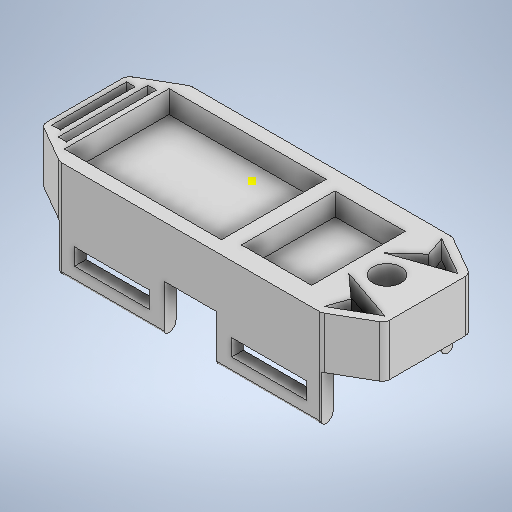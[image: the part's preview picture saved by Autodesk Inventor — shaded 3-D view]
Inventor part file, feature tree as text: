
AUTODESK INVENTOR PART (.ipt)
format: ipt  version: 2025.1 (Build 291241000, 241)  size: 457,216 bytes
history: native  units: mm
features: extrude x6, sketch x6, fillet x3
ambient origin geometry x8: Origin, YZ Plane, XZ Plane, XY Plane, X Axis, Y Axis, Z Axis, Center Point
bodies: Solid1 (feature_tree)
feature tree (15):
  extrude  "Extrusion1"  Depth=140.0mm
  sketch  "Sketch2"  dims[d9=30.0deg d10=30.0deg]
  sketch  "Sketch3"  dims[d11=25.0mm d12=25.0mm]
  extrude  "Extrusion2"  TaperAngle=30.0deg  [1 undecoded]
  extrude  "Extrusion3"  Depth=25.0mm
  extrude  "Extrusion4"  TaperAngle=150.0deg  [1 undecoded]
  extrude  "Extrusion5"  Depth=25.0mm
  extrude  "Extrusion6"  Depth=2.0mm
  fillet  "Fillet1"  Radius=84.0mm
  fillet  "Fillet2"  Radius=56.0mm
  fillet  "Fillet3"  Radius=37.5mm
  sketch  "Sketch1"  dims[d0=70.0mm d6=140.0mm]
  sketch  "Sketch4"  dims[d13=150.0deg d14=150.0deg]
  sketch  "Sketch5"  dims[d15=25.0mm d16=25.0mm]
  sketch  "Sketch6"  dims[d17=45.0mm d18=45.0mm d22=84.0mm d23=56.0mm d24=37.5mm d25=50.0mm d26=15.0mm d27=35.0mm d28=35.0mm d29=27.5mm d30=0.0mm d31=56.0mm d32=84.0mm d33=37.5mm d34=50.0mm d35=7.0mm d36=7.0mm d37=10.0mm d38=10.0mm d43=4.5mm d44=40.0mm d45=4.5mm d47=48.0mm d51=0.0mm d55=12.0mm d56=0.0mm d57=10.0mm d58=0.0mm d59=57.5mm d60=69.0mm d61=6.25mm d62=6.25mm d63=10.0mm d64=0.0mm d65=9.0mm d66=40.0mm d67=8.0mm d68=8.0mm d69=8.0mm d70=8.0mm d72=8.0mm d73=9.0mm d74=8.0mm d75=8.0mm d76=8.0mm d77=56.0mm d78=40.0mm d79=25.0mm d80=25.0mm d81=6.25mm d82=0.0mm d83=8.0mm d84=8.0mm d85=9.0mm d86=6.25mm d87=0.0mm d88=4.0mm d89=4.0mm d90=2.0mm d53=0.5mm d54=0.872665mm d91=0.0mm d92=0.0mm]
note: 2 required parameter values undecoded (feature->parameter linkage not recoverable at this tier; creation-order binding heuristic only, values carry confidence <= 0.55)
